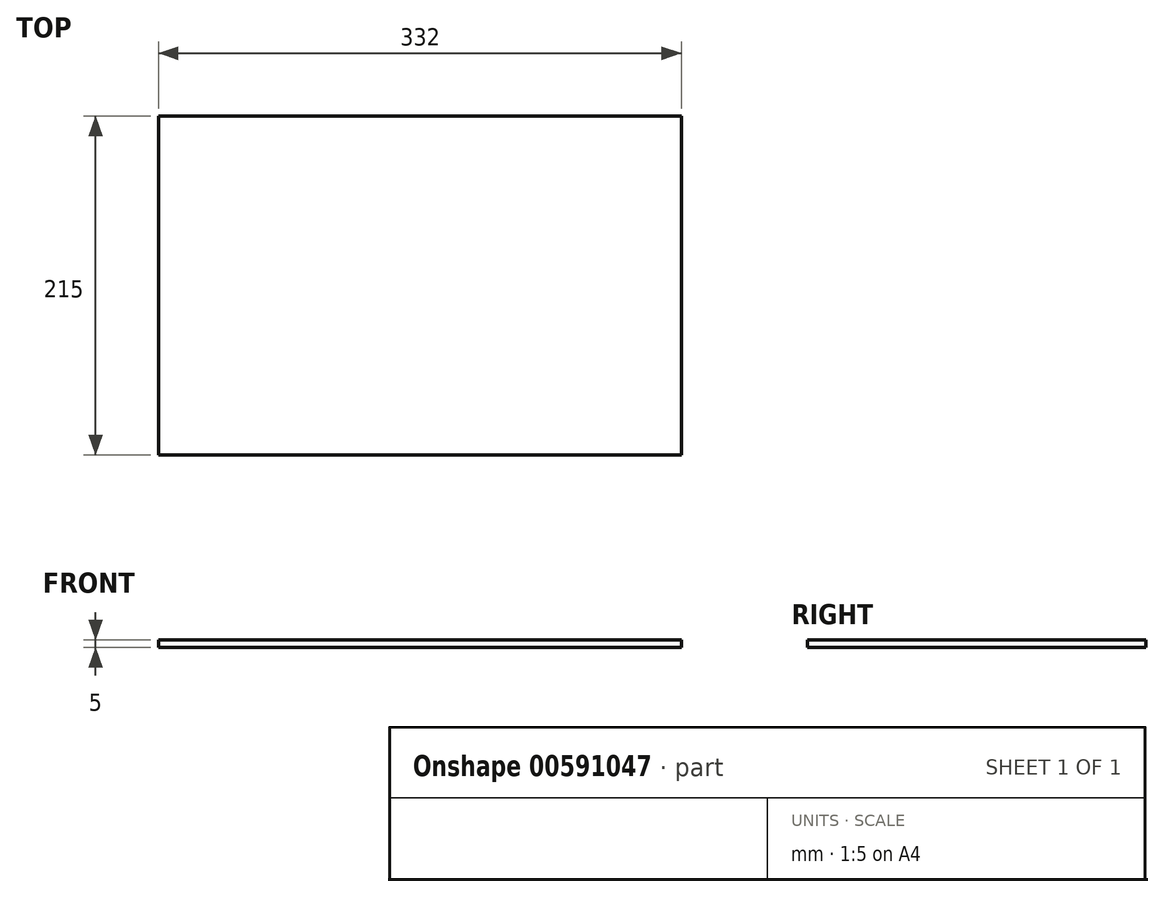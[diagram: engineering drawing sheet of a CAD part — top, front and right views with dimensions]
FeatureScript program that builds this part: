
annotation { "Feature Type Name" : "Feature", "Feature Type Description" : "" }
export const myFeature = defineFeature(function(context is Context, id is Id, definition is map)
    precondition{}
    {
        {
            var Q0;
            Q0=qCreatedBy(makeId("Top.planeOp"),FACE);
            var sketch = newSketch(context, id + "F0", { "sketchPlane" : qUnion([Q0])});
            skLineSegment(sketch, "E0.bottom", {"start": v(166, 107.5) * mm, "end": v(-166, 107.5) * mm});
            skLineSegment(sketch, "E0.top", {"start": v(166, -107.5) * mm, "end": v(-166, -107.5) * mm});
            skLineSegment(sketch, "E0.left", {"start": v(166, 107.5) * mm, "end": v(166, -107.5) * mm});
            skLineSegment(sketch, "E0.right", {"start": v(-166, 107.5) * mm, "end": v(-166, -107.5) * mm});
            skPoint(sketch, "E0.middle", {"position": v(0, 0) * mm});
            skSolve(sketch);
        }
        {
            var Q0;
            Q0 = qSketchRegion(id + "F0", true);
            extrude(context, id + "F1", {"entities" : qUnion([Q0]), "endBound" : BoundingType.SYMMETRIC, "depth" : 5 * mm, "offsetDistance" : 25 * mm});
        }
    });
